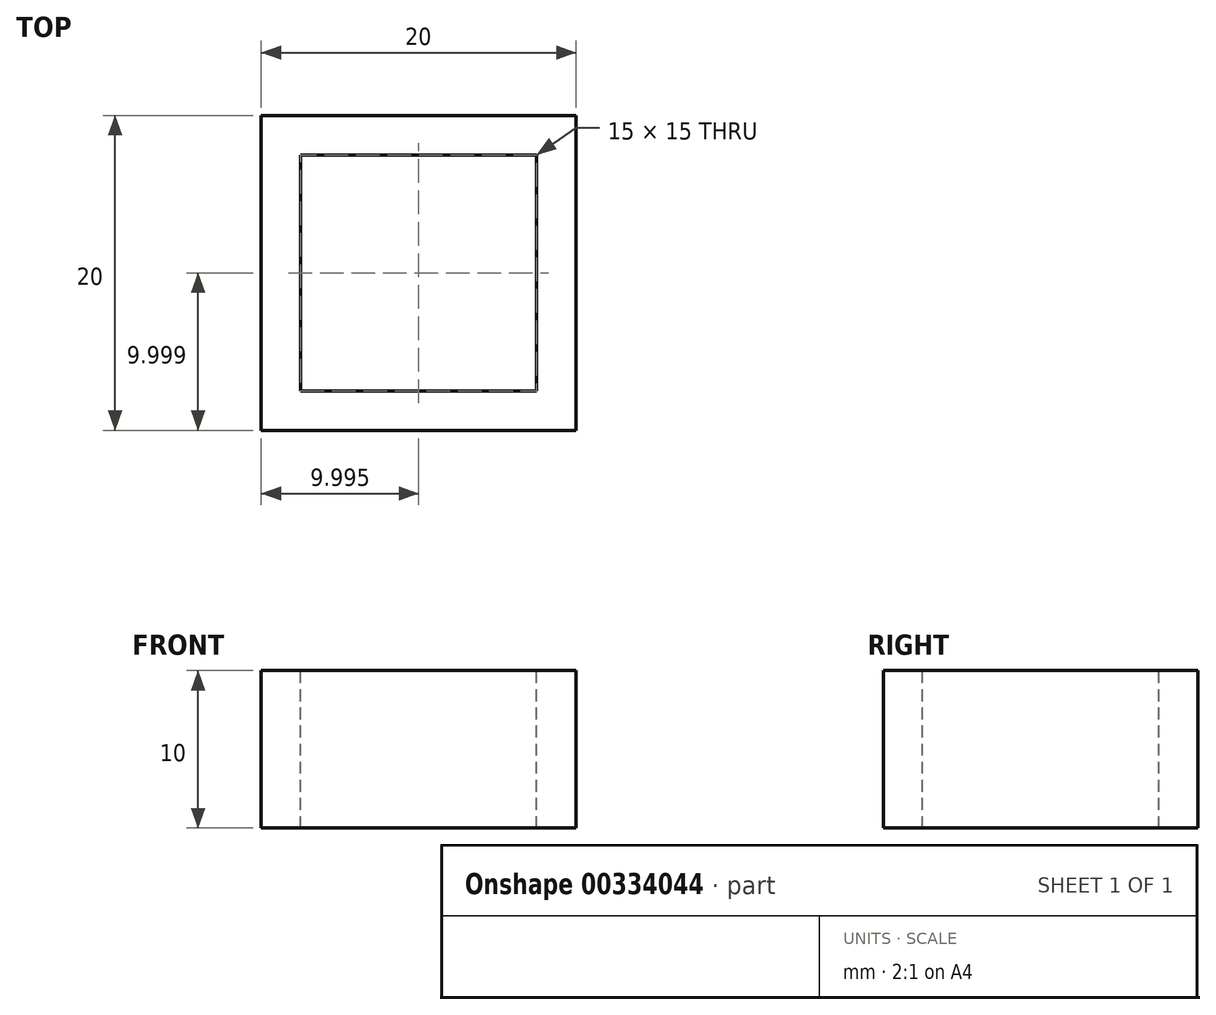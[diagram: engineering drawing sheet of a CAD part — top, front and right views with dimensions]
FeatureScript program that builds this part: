
annotation { "Feature Type Name" : "Feature", "Feature Type Description" : "" }
export const myFeature = defineFeature(function(context is Context, id is Id, definition is map)
    precondition{}
    {
        {
            var Q0;
            Q0=qCreatedBy(makeId("Top.planeOp"),FACE);
            var sketch = newSketch(context, id + "F0", { "sketchPlane" : qUnion([Q0])});
            skCircle(sketch, "E0", {"center": v(0, 0) * mm, "radius": 7.5 * mm});
            skSolve(sketch);
        }
        {
            var Q0;
            Q0 = qSketchRegion(id + "F0", true);
            extrude(context, id + "F1", {"entities" : qUnion([Q0]), "depth" : 0.4 * mm});
        }
        {
            var Q0;
            Q0=makeQuery(id+"F1.opExtrude","SWEPT_BODY",BODY,{"disambiguationData":[OSD([sQuery(id+"F0.wireOp",EDGE,"E0")])]});
            deleteBodies(context, id + "F2", {"entities" : qUnion([Q0])});
        }
        {
            var Q0;
            Q0=qCreatedBy(makeId("Top.planeOp"),FACE);
            var sketch = newSketch(context, id + "F3", { "sketchPlane" : qUnion([Q0])});
            skLineSegment(sketch, "E1.bottom", {"start": v(-23.52, 19.93) * mm, "end": v(-3.52, 19.93) * mm});
            skLineSegment(sketch, "E1.top", {"start": v(-23.52, -0.07) * mm, "end": v(-3.52, -0.07) * mm});
            skLineSegment(sketch, "E1.left", {"start": v(-23.52, 19.93) * mm, "end": v(-23.52, -0.07) * mm});
            skLineSegment(sketch, "E1.right", {"start": v(-3.52, 19.93) * mm, "end": v(-3.52, -0.07) * mm});
            skSolve(sketch);
        }
        {
            var Q0;
            Q0 = qSketchRegion(id + "F3", true);
            extrude(context, id + "F4", {"entities" : qUnion([Q0]), "depth" : 10 * mm});
        }
        {
            var Q0;
            Q0=makeQuery(id+"F4.opExtrude","CAP_FACE",FACE,{"disambiguationData":[OSD([sQuery(id+"F3.wireOp",EDGE,"E1.bottom"),sQuery(id+"F3.wireOp",EDGE,"E1.top"),sQuery(id+"F3.wireOp",EDGE,"E1.left"),sQuery(id+"F3.wireOp",EDGE,"E1.right")])],"isStart":false});
            var sketch = newSketch(context, id + "F5", { "sketchPlane" : qUnion([Q0])});
            skLineSegment(sketch, "E2", {"start": v(-23.52, 19.93) * mm, "end": v(-21.02, 19.93) * mm});
            skLineSegment(sketch, "E3", {"start": v(-21.02, 19.93) * mm, "end": v(-21.02, 17.43) * mm});
            skLineSegment(sketch, "E4.bottom", {"start": v(-21.02, 17.43) * mm, "end": v(-6.02, 17.43) * mm});
            skLineSegment(sketch, "E4.top", {"start": v(-21.02, 2.43) * mm, "end": v(-6.02, 2.43) * mm});
            skLineSegment(sketch, "E4.left", {"start": v(-21.02, 17.43) * mm, "end": v(-21.02, 2.43) * mm});
            skLineSegment(sketch, "E4.right", {"start": v(-6.02, 17.43) * mm, "end": v(-6.02, 2.43) * mm});
            skSolve(sketch);
        }
        {
            var Q0;
            Q0 = qSketchRegion(id + "F5", true);
            extrude(context, id + "F6", {"entities" : qUnion([Q0]), "operationType" : NewBodyOperationType.REMOVE, "oppositeDirection" : true, "depth" : 25 * mm});
        }
    });
